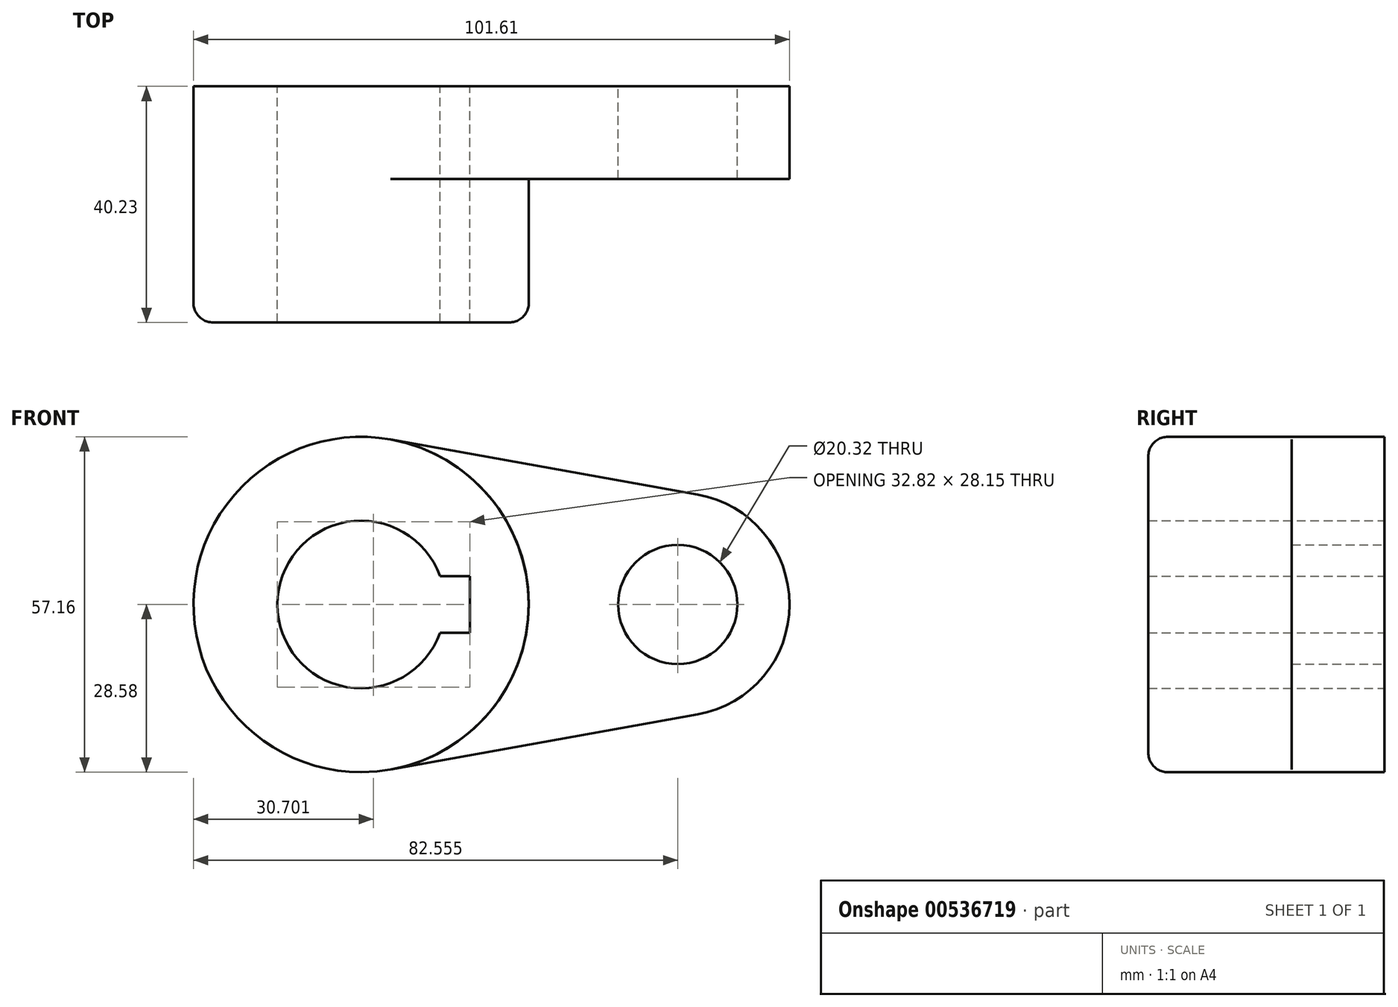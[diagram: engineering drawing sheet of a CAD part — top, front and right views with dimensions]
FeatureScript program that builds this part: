
annotation { "Feature Type Name" : "Feature", "Feature Type Description" : "" }
export const myFeature = defineFeature(function(context is Context, id is Id, definition is map)
    precondition{}
    {
        {
            var Q0;
            Q0=qCreatedBy(makeId("Front.planeOp"),FACE);
            var sketch = newSketch(context, id + "F0", { "sketchPlane" : qUnion([Q0])});
            skCircle(sketch, "E0", {"center": v(0, 0) * mm, "radius": 28.57 * mm});
            skArc(sketch, "E1", {"start": v(57.34, -18.75) * mm, "mid": v(73.03, 0) * mm, "end": v(57.34, 18.75) * mm});
            skLineSegment(sketch, "E2", {"start": v(5.04, 28.13) * mm, "end": v(57.34, 18.75) * mm});
            skLineSegment(sketch, "E3", {"start": v(5.04, -28.13) * mm, "end": v(57.34, -18.75) * mm});
            skCircle(sketch, "E4", {"center": v(53.98, 0) * mm, "radius": 10.16 * mm});
            skPoint(sketch, "E5.middle", {"position": v(28.57, 0) * mm});
            skArc(sketch, "E6", {"start": v(13.45, 4.83) * mm, "mid": v(-14.29, 0) * mm, "end": v(13.45, -4.83) * mm});
            skLineSegment(sketch, "E7.bottom", {"start": v(18.53, 4.83) * mm, "end": v(13.45, 4.83) * mm});
            skLineSegment(sketch, "E7.top", {"start": v(18.53, -4.83) * mm, "end": v(13.45, -4.83) * mm});
            skLineSegment(sketch, "E7.left", {"start": v(18.53, 4.83) * mm, "end": v(18.53, -4.83) * mm});
            skPoint(sketch, "E7.middle", {"position": v(14.29, 0) * mm});
            skLineSegment(sketch, "E8", {"start": v(18.53, 0) * mm, "end": v(0, 0) * mm, "construction": true});
            skSolve(sketch);
        }
        {
            var Q0;
            Q0=makeQuery(id+"F0.imprint","IMPRINT",FACE,{"disambiguationData":[TD([[makeQuery(id+"F0.imprint","IMPRINT",EDGE,{"derivedFrom":sQuery(id+"F0.wireOp",EDGE,"E6")}),-1.0]])]});
            extrude(context, id + "F1", {"entities" : qUnion([Q0]), "depth" : 40.23 * mm, "offsetDistance" : 25.4 * mm});
        }
        {
            var Q0;
            Q0=makeQuery(id+"F0.imprint","IMPRINT",FACE,{"disambiguationData":[TD([[makeQuery(id+"F0.imprint","IMPRINT",EDGE,{"derivedFrom":sQuery(id+"F0.wireOp",EDGE,"E1")}),1.0]])]});
            extrude(context, id + "F2", {"entities" : qUnion([Q0]), "operationType" : NewBodyOperationType.ADD, "depth" : 15.77 * mm, "offsetDistance" : 25.4 * mm});
        }
        {
            var Q0;
            Q0=makeQuery(id+"F1.opExtrude","CAP_EDGE",EDGE,{"disambiguationData":[OSD([sQuery(id+"F0.wireOp",EDGE,"E0")])],"isStart":false});
            fillet(context, id + "F3", {"entities" : qUnion([Q0]), "radius" : 3.3 * mm, "tangentPropagation" : true, "allowEdgeOverflow" : false});
        }
    });
